# Revit family: Hager-PABLO-Surface_mounted-IP40-With_Cover-Without_DIN-Hosted-IT-it
name_source: partatom
category: Electrical Equipment
units: mm (PartAtom-declared; Revit-internal decimal feet)

## family parameters
Cut with Voids When Loaded = No
Host = Face
Maintain Annotation Orientation = Yes
Panel Configuration = Two Columns, Circuits Across
Part Type = Panelboard
Room Calculation Point = No
Round Connector Dimension = Use Diameter
Shared = No

## types (6) — shared parameters
BC_MODEL_ID = 1554427
BC_OBJECT_ID = 513915
BC_OBJECT_VERSION = #3
Code hager = ADD-EC000214_EU
EF000003 - Tipo di montaggio = A parete
EF000024 - Resistente ai raggi UV = No
EF000118 - Con piastra di montaggio = No
EF001062 - Esecuzione EMC = No
EF001088 - Possibilità di applicazione = No
EF001134 - Barra DIN = No
EF005474 - Grado di protezione (IP) = IP40
EF006244 - Coperchio/porta trasparente = No
EF006306 - Con serratura = No
EF015776 - Morsettiera di terra = No
EF015777 - Morsettiera neutra = No
EF015941 - Segnale di passaggio porta = No
ETIM class code = EC000214
ETIM class name = Small distribution board
HG000001 - Numero di colonne = 1
HG000002-with door or cover-it = Yes
HG000003-Range-it = PABLO
HG000005-Thickness-it = 2 mm  [stored 0.00656168 ft]
HG000006-Flush mounted-it = No
HG000009-Double swing door-it = No
HG000010-Asymmetric doors-it = No
HG000011-Empty rows from bottom-it = No
HG000012-Door swing angle-it = 90.00°
HG000013-Door on the left-it = No
HG000014-Door on the right-it = Yes
HG000015-Clearance visibility-it = Yes
HG000016-Door 3D visibility-it = Yes
HG000017-Distance between poles-it = 18 mm  [stored 0.0590551 ft]
HG000099-Onfly Template ID-it-IT = 507532
Manufacturer = Hager
Name = PABLO-Surface_mounted-IP40-With_Cover-Without_DIN-IT
Name BIM&CO = Electricity
Name hager = ADD_Enclosures_EC000214
Uniformat = Low Tension Service & Dist.
Uniformat code = D501001
zero-valued in all types: Default Elevation, EF000218 - Profondità di incasso, EF000332 - Altezza della parte incassata, EF000846 - Larghezza di montaggio, EF001131 - Profondità interna, HG000007-Number of empty columns-it, HG000008-Number of empty rows-it

## per-type parameters (varying)
| type | BC_VARIANT_ID | EF000008 - Larghezza | EF000040 - Altezza | EF000049 - Profondità | EF000116 - Numero RAL | EF000266 - Numero di file | EF002950 - Numero moduli DIN | HG000004-Manufacturer reference-it | HG000060-RAL-number | HGEF000266-Numero di file | HGEF0002950-Numero moduli DIN |
| PABLO-Surface_mounted_W408_H625_D137_18_Modular_Spacing-B04022 | 1179094 | 408 mm | 625 mm  [stored 2.05052 ft] | 137 mm  [stored 0.449475 ft] | 7035 | 3 | 18 | B04022 | 7035 | 3 | 18 |
| PABLO-Surface_mounted_W210_H200_D103_8_Modular_Spacing-B04083 | 1179095 | 210 mm  [stored 0.688976 ft] | 200 mm  [stored 0.656168 ft] | 103 mm  [stored 0.337927 ft] | 9001 | 1 | 8 | B04083 | 9001 | 1 | 8 |
| PABLO-Surface_mounted_W300_H250_D113_12_Modular_Spacing-B04084 | 1179096 | 300 mm | 250 mm  [stored 0.82021 ft] | 113 mm  [stored 0.370735 ft] | 9001 | 1 | 12 | B04084 | 9001 | 1 | 12 |
| PABLO-Surface_mounted_W408_H275_D137_18_Modular_Spacing-B04085 | 1179097 | 408 mm | 275 mm | 137 mm  [stored 0.449475 ft] | 9001 | 1 | 18 | B04085 | 9001 | 1 | 18 |
| PABLO-Surface_mounted_W300_H400_D113_12_Modular_Spacing-B04086 | 1179098 | 300 mm | 400 mm  [stored 1.31234 ft] | 113 mm  [stored 0.370735 ft] | 9001 | 2 | 12 | B04086 | 9001 | 2 | 12 |
| PABLO-Surface_mounted_W408_H625_D137_18_Modular_Spacing-B04090 | 1179099 | 408 mm | 625 mm  [stored 2.05052 ft] | 137 mm  [stored 0.449475 ft] | 9001 | 3 | 18 | B04090 | 9001 | 3 | 18 |

note: column(s) folded — value = type name in every type: Reference

note: [stored X ft] marks values corroborated as IEEE doubles in the binary element streams (Revit-internal decimal feet)

## geometry (parser evidence)
native form markers: Sweep x13
no freeform markers — native parametric forms only
